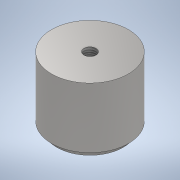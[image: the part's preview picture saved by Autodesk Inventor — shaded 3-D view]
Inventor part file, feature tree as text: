
AUTODESK INVENTOR PART (.ipt)
format: ipt  version: 2022 (Build 260153000, 153)  size: 114,688 bytes
history: native  units: in
note: dims shown in document units (in); Inventor stores cm internally (conversion verified against a paired STEP export)
features: sketch x3, extrude x2, hole x1, thread x1
ambient origin geometry x8: Origin, YZ Plane, XZ Plane, XY Plane, X Axis, Y Axis, Z Axis, Center Point
bodies: Solid1 (feature_tree)
feature tree (7):
  extrude  "Extrusion1"  Depth=0.7874in TaperAngle=0.0deg
  extrude  "Extrusion2"  Depth=0.0787in TaperAngle=0.0deg
  hole  "Hole1"  [1 undecoded]
  thread  "Thread1"  [1 undecoded]
  sketch  "Sketch1"  dims[d0=1.0039in d1=0.7874in d2=0.0in]
  sketch  "Sketch2"  dims[d3=0.8661in d4=0.0787in d5=0.0in]
  sketch  "Sketch3"  dims[d6=0.1575in d7=0.2362in d8=0.1575in d9=0.0787in d10=90.0deg d11=0.1969in d12=0.0in d13=0.1969in d14=0.0in]
note: 2 required parameter values undecoded (feature->parameter linkage not recoverable at this tier; creation-order binding heuristic only, values carry confidence <= 0.55)
